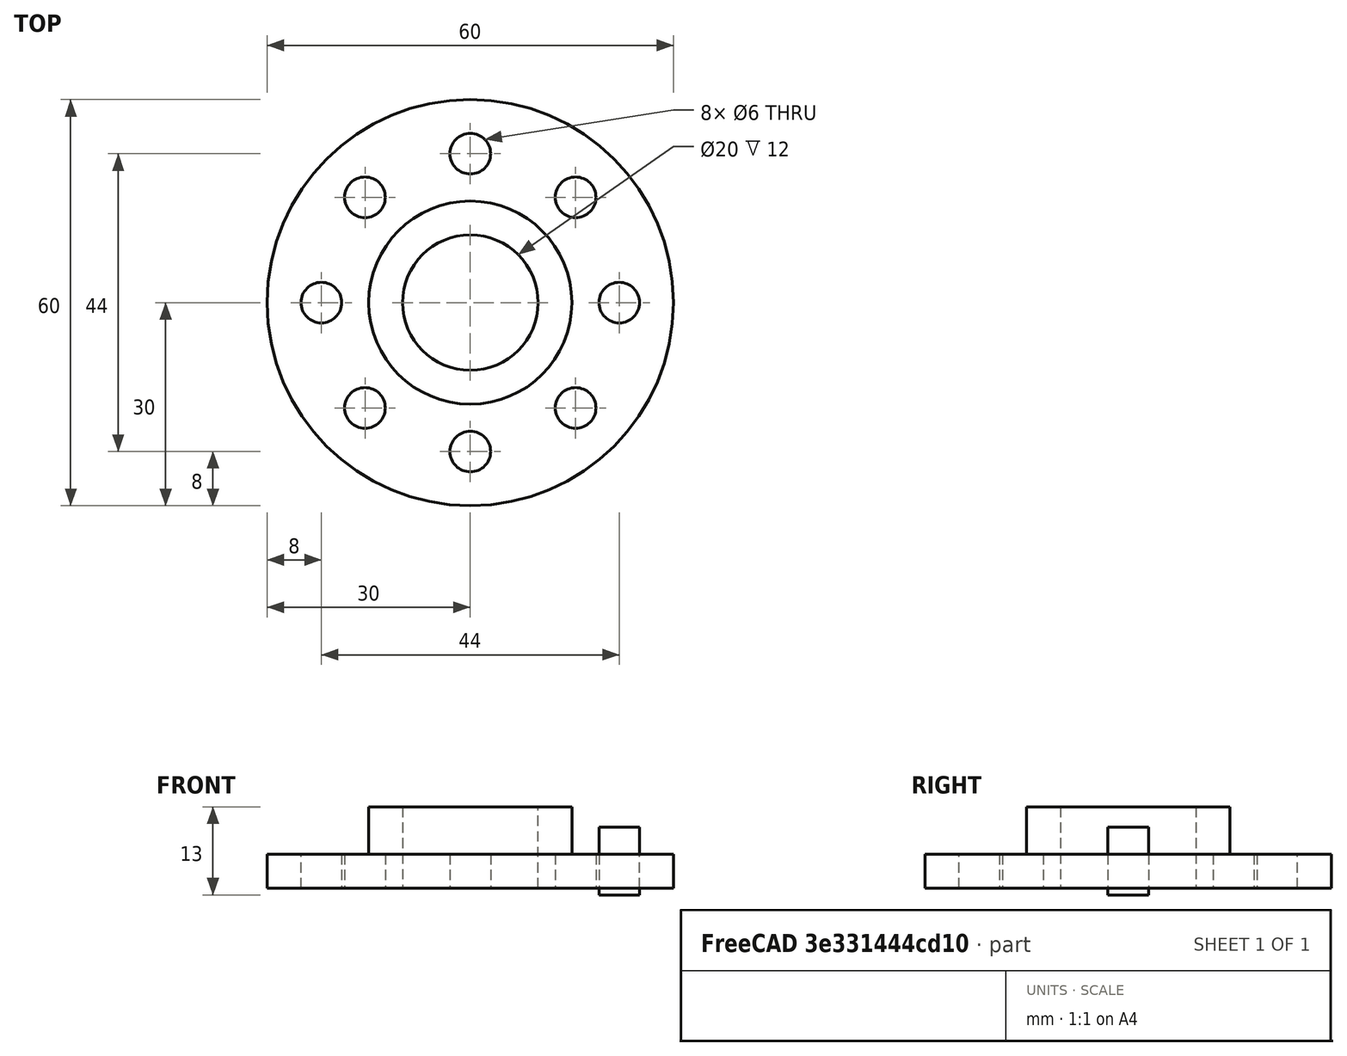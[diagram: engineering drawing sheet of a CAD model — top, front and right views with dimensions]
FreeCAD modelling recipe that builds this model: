
FCSTD DOCUMENT  (FreeCAD 1.0R39319 (Git))
Label: ojt1_t11p01_flange
License: All rights reserved
LicenseURL: https://en.wikipedia.org/wiki/All_rights_reserved
objects: Part::Cylinder×4, Part::Cut×2, Part::MultiFuse×1, Part::FeaturePython×1
note: 7 computed .brp shape members not serialized (recipe doc carries the construction recipe); baked Part::Feature solids carry a one-line shape summary decoded from their .brp

FEATURE [Part::Cylinder] Cylinder  label="Cilindre"
  Angle = 360
  AttacherType = Attacher::AttachEngine3D
  FirstAngle = 0
  Height = 5
  Radius = 30
  SecondAngle = 0
FEATURE [Part::Cylinder] Cylinder001  label="Cilindre001"
  Angle = 360
  AttacherType = Attacher::AttachEngine3D
  FirstAngle = 0
  Height = 12
  Radius = 15
  SecondAngle = 0
FEATURE [Part::MultiFuse] Fusion
  Refine = true
  Shapes = -> [Cylinder001,Cylinder]
FEATURE [Part::Cylinder] Cylinder002  label="Cilindre002"
  Angle = 360
  AttacherType = Attacher::AttachEngine3D
  FirstAngle = 0
  Height = 30
  Placement = pos=(0,0,-1) rot=(0,0,1;0rad)
  Radius = 10
  SecondAngle = 0
FEATURE [Part::Cut] Cut
  Base = -> Fusion
  Refine = true
  Tool = -> Cylinder002
FEATURE [Part::Cylinder] Cylinder003  label="Cilindre003"
  Angle = 360
  AttacherType = Attacher::AttachEngine3D
  FirstAngle = 0
  Height = 10
  Placement = pos=(22,0,-1) rot=(0,0,1;0rad)
  Radius = 3
  SecondAngle = 0
FEATURE [Part::FeaturePython] Array  # Draft array (typed FeaturePython)
  AlwaysSyncPlacement = false
  Angle = 360
  ArrayType = 1
  Axis = (0,0,1)
  Base = -> Cylinder003
  Center = (0,0,0)
  Count = 8
  ExpandArray = false
  Fuse = false
  IntervalAxis = (0,0,0)
  IntervalX = (50,0,0)
  IntervalY = (0,50,0)
  IntervalZ = (0,0,50)
  NumberCircles = 3
  NumberPolar = 8
  NumberX = 2
  NumberY = 2
  NumberZ = 1
  PlacementList = 8 placements: [(22,0,-1),(15.5563,15.5563,-1),(0,22,-1),(-15.5563,15.5563,-1),(-22,2.69422e-15,-1),(-15.5563,-15.5563,-1),(-4.88498e-15,-22,-1),(15.5563,-15.5563,-1)]
  RadialDistance = 50
  ScaleList = (8) [(1,1,1),(1,1,1),(1,1,1),(1,1,1),(1,1,1),(1,1,1),(1,1,1),(1,1,1)]
  Symmetry = 1
  TangentialDistance = 25
FEATURE [Part::Cut] Cut001
  Base = -> Cut
  Refine = true
  Tool = -> Array
